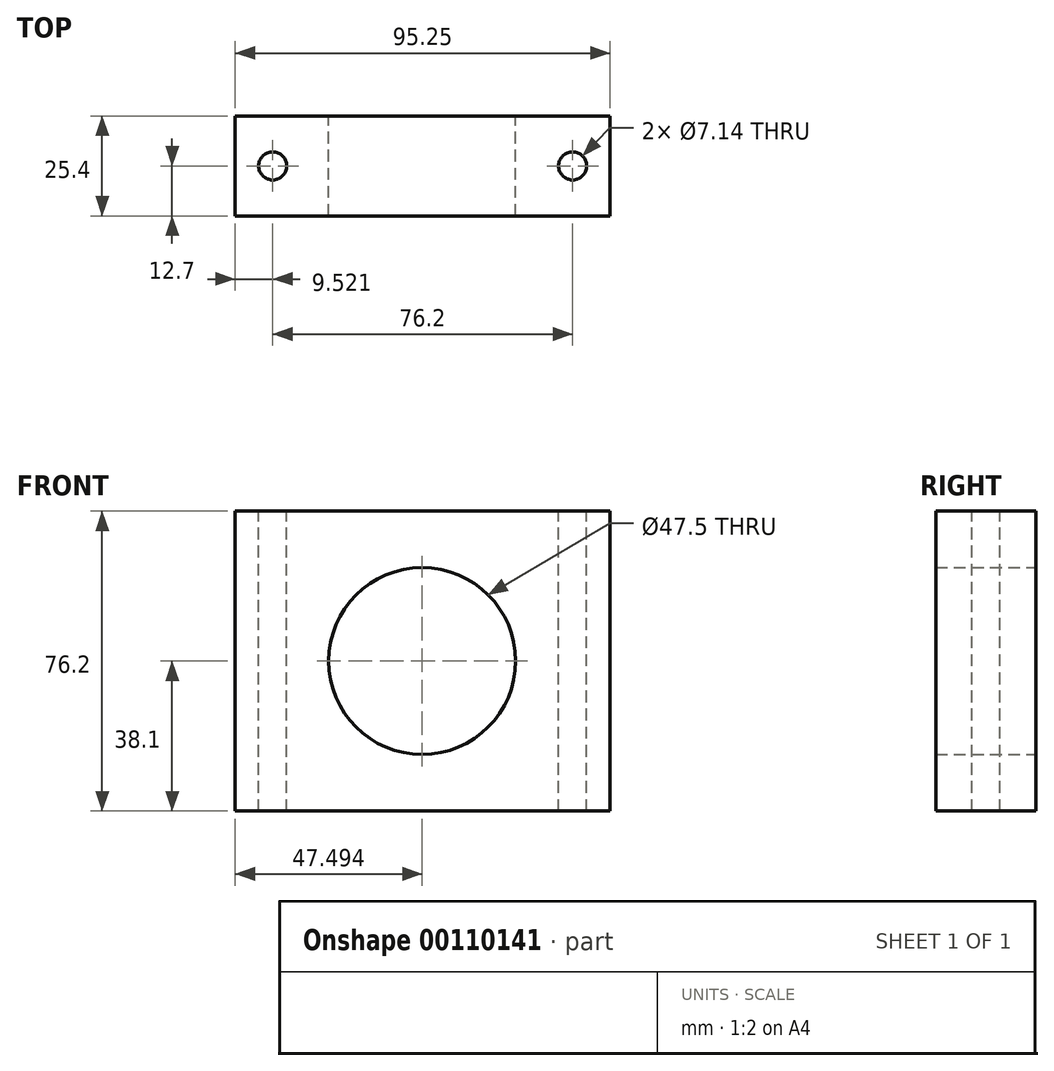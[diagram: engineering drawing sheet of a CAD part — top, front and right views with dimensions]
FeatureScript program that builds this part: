
annotation { "Feature Type Name" : "Feature", "Feature Type Description" : "" }
export const myFeature = defineFeature(function(context is Context, id is Id, definition is map)
    precondition{}
    {
        {
            var Q0;
            Q0=qCreatedBy(makeId("Front.planeOp"),FACE);
            var sketch = newSketch(context, id + "F0", { "sketchPlane" : qUnion([Q0])});
            skLineSegment(sketch, "E0", {"start": v(-48.57, 0) * mm, "end": v(46.68, 0) * mm});
            skLineSegment(sketch, "E1", {"start": v(-1.08, 0) * mm, "end": v(-1.08, 76.2) * mm, "construction": true});
            skLineSegment(sketch, "E2", {"start": v(-48.57, 38.1) * mm, "end": v(46.68, 38.1) * mm, "construction": true});
            skLineSegment(sketch, "E3", {"start": v(46.68, 0) * mm, "end": v(46.68, 76.2) * mm});
            skLineSegment(sketch, "E4", {"start": v(46.68, 76.2) * mm, "end": v(-1.08, 76.2) * mm});
            skLineSegment(sketch, "E5", {"start": v(-1.08, 76.2) * mm, "end": v(-48.57, 76.2) * mm});
            skLineSegment(sketch, "E6", {"start": v(-48.57, 76.2) * mm, "end": v(-48.57, 0) * mm});
            skCircle(sketch, "E7", {"center": v(-1.08, 38.1) * mm, "radius": 23.75 * mm});
            skSolve(sketch);
        }
        {
            var Q0;
            Q0 = qSketchRegion(id + "F0", true);
            extrude(context, id + "F1", {"entities" : qUnion([Q0]), "depth" : 25.4 * mm});
        }
        {
            var Q0;
            Q0=makeQuery(id+"F1.opExtrude","SWEPT_FACE",FACE,{"disambiguationData":[OSD([sQuery(id+"F0.wireOp",EDGE,"E4"),sQuery(id+"F0.wireOp",EDGE,"E5")])]});
            var sketch = newSketch(context, id + "F2", { "sketchPlane" : qUnion([Q0])});
            skLineSegment(sketch, "E8", {"start": v(37.15, 0) * mm, "end": v(37.15, -25.4) * mm, "construction": true});
            skLineSegment(sketch, "E9", {"start": v(-48.57, -12.7) * mm, "end": v(46.68, -12.7) * mm, "construction": true});
            skLineSegment(sketch, "E10", {"start": v(-39.05, 0) * mm, "end": v(-39.05, -25.4) * mm, "construction": true});
            skCircle(sketch, "E11", {"center": v(-39.05, -12.7) * mm, "radius": 3.57 * mm});
            skCircle(sketch, "E12", {"center": v(37.15, -12.7) * mm, "radius": 3.57 * mm});
            skSolve(sketch);
        }
        {
            var Q0;
            Q0=makeQuery(id+"F2.imprint","IMPRINT",FACE,{"disambiguationData":[TD([[makeQuery(id+"F2.imprint","IMPRINT",EDGE,{"derivedFrom":sQuery(id+"F2.wireOp",EDGE,"E11")}),1.0]])]});
            var Q1;
            Q1=makeQuery(id+"F2.imprint","IMPRINT",FACE,{"disambiguationData":[TD([[makeQuery(id+"F2.imprint","IMPRINT",EDGE,{"derivedFrom":sQuery(id+"F2.wireOp",EDGE,"E12")}),1.0]])]});
            extrude(context, id + "F3", {"entities" : qUnion([Q0, Q1]), "operationType" : NewBodyOperationType.REMOVE, "oppositeDirection" : true, "depth" : 76.2 * mm});
        }
    });
